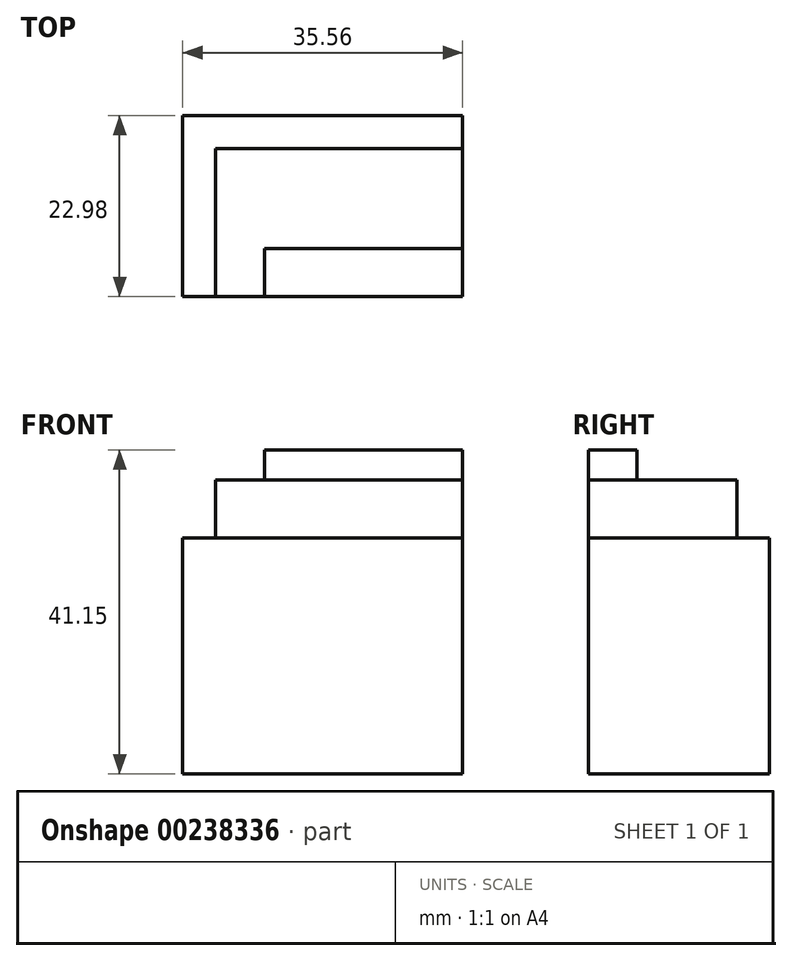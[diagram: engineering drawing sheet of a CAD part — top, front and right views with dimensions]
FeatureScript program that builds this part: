
annotation { "Feature Type Name" : "Feature", "Feature Type Description" : "" }
export const myFeature = defineFeature(function(context is Context, id is Id, definition is map)
    precondition{}
    {
        {
            var Q0;
            Q0=qCreatedBy(makeId("Top.planeOp"),FACE);
            var sketch = newSketch(context, id + "F0", { "sketchPlane" : qUnion([Q0])});
            skLineSegment(sketch, "E0.bottom", {"start": v(0, 0) * mm, "end": v(-35.56, 0) * mm});
            skLineSegment(sketch, "E0.top", {"start": v(0, 22.98) * mm, "end": v(-35.56, 22.98) * mm});
            skLineSegment(sketch, "E0.left", {"start": v(0, 0) * mm, "end": v(0, 22.98) * mm});
            skLineSegment(sketch, "E0.right", {"start": v(-35.56, 0) * mm, "end": v(-35.56, 22.98) * mm});
            skSolve(sketch);
        }
        {
            var Q0;
            Q0 = qSketchRegion(id + "F0", true);
            extrude(context, id + "F1", {"entities" : qUnion([Q0]), "depth" : 29.97 * mm});
        }
        {
            var Q0;
            Q0=makeQuery(id+"F1.opExtrude","CAP_FACE",FACE,{"disambiguationData":[OSD([sQuery(id+"F0.wireOp",EDGE,"E0.bottom"),sQuery(id+"F0.wireOp",EDGE,"E0.top"),sQuery(id+"F0.wireOp",EDGE,"E0.left"),sQuery(id+"F0.wireOp",EDGE,"E0.right")])],"isStart":false});
            var sketch = newSketch(context, id + "F2", { "sketchPlane" : qUnion([Q0])});
            skLineSegment(sketch, "E1.bottom", {"start": v(0, 0) * mm, "end": v(-31.4, 0) * mm});
            skLineSegment(sketch, "E1.top", {"start": v(0, 18.82) * mm, "end": v(-31.4, 18.82) * mm});
            skLineSegment(sketch, "E1.left", {"start": v(0, 0) * mm, "end": v(0, 18.82) * mm});
            skLineSegment(sketch, "E1.right", {"start": v(-31.4, 0) * mm, "end": v(-31.4, 18.82) * mm});
            skSolve(sketch);
        }
        {
            var Q0;
            Q0 = qSketchRegion(id + "F2", true);
            extrude(context, id + "F3", {"entities" : qUnion([Q0]), "depth" : 7.37 * mm});
        }
        {
            var Q0;
            Q0=makeQuery(id+"F3.opExtrude","CAP_FACE",FACE,{"disambiguationData":[OSD([sQuery(id+"F2.wireOp",EDGE,"E1.bottom"),sQuery(id+"F2.wireOp",EDGE,"E1.top"),sQuery(id+"F2.wireOp",EDGE,"E1.left"),sQuery(id+"F2.wireOp",EDGE,"E1.right")])],"isStart":false});
            var sketch = newSketch(context, id + "F4", { "sketchPlane" : qUnion([Q0])});
            skLineSegment(sketch, "E2.bottom", {"start": v(0, 0) * mm, "end": v(-25.17, 0) * mm});
            skLineSegment(sketch, "E2.top", {"start": v(0, 6.12) * mm, "end": v(-25.17, 6.12) * mm});
            skLineSegment(sketch, "E2.left", {"start": v(0, 0) * mm, "end": v(0, 6.12) * mm});
            skLineSegment(sketch, "E2.right", {"start": v(-25.17, 0) * mm, "end": v(-25.17, 6.12) * mm});
            skSolve(sketch);
        }
        {
            var Q0;
            Q0 = qSketchRegion(id + "F4", true);
            extrude(context, id + "F5", {"entities" : qUnion([Q0]), "depth" : 3.8 * mm});
        }
    });
